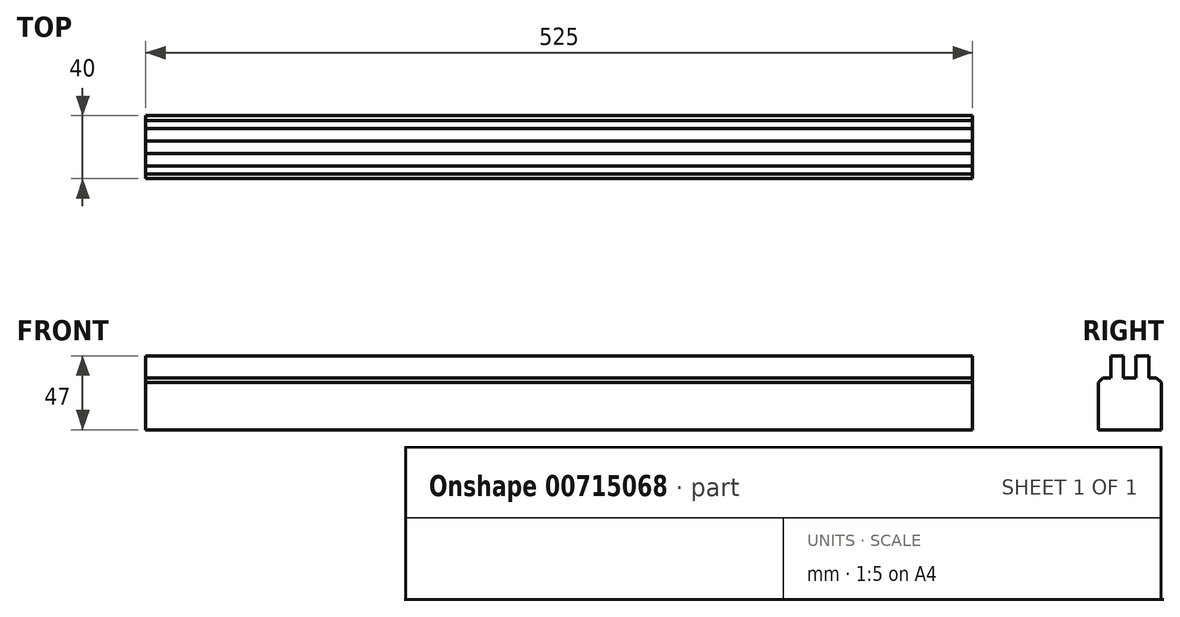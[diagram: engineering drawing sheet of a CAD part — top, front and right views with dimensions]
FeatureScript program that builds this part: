
annotation { "Feature Type Name" : "Feature", "Feature Type Description" : "" }
export const myFeature = defineFeature(function(context is Context, id is Id, definition is map)
    precondition{}
    {
        {
            var Q0;
            Q0=qCreatedBy(makeId("Right.planeOp"),FACE);
            var sketch = newSketch(context, id + "F0", { "sketchPlane" : qUnion([Q0])});
            skLineSegment(sketch, "E0", {"start": v(20, 63) * mm, "end": v(20, -63) * mm});
            skLineSegment(sketch, "E1", {"start": v(20, -63) * mm, "end": v(17, -66) * mm});
            skLineSegment(sketch, "E2", {"start": v(17, -66) * mm, "end": v(12, -66) * mm});
            skLineSegment(sketch, "E3", {"start": v(12, -52) * mm, "end": v(12, -66) * mm});
            skLineSegment(sketch, "E4", {"start": v(12, -52) * mm, "end": v(4, -52) * mm});
            skLineSegment(sketch, "E5", {"start": v(4, -66) * mm, "end": v(4, -52) * mm});
            skLineSegment(sketch, "E6", {"start": v(4, -66) * mm, "end": v(-4, -66) * mm});
            skLineSegment(sketch, "E7", {"start": v(-4, -52) * mm, "end": v(-4, -66) * mm});
            skLineSegment(sketch, "E8", {"start": v(-4, -52) * mm, "end": v(-12, -52) * mm});
            skLineSegment(sketch, "E9", {"start": v(-12, -66) * mm, "end": v(-12, -52) * mm});
            skLineSegment(sketch, "E10", {"start": v(-12, -66) * mm, "end": v(-17, -66) * mm});
            skLineSegment(sketch, "E11", {"start": v(-17, -66) * mm, "end": v(-20, -63) * mm});
            skLineSegment(sketch, "E12", {"start": v(-20, -63) * mm, "end": v(-20, 63) * mm});
            skLineSegment(sketch, "E13", {"start": v(-20, 63) * mm, "end": v(-17, 66) * mm});
            skLineSegment(sketch, "E14", {"start": v(-17, 66) * mm, "end": v(-12, 66) * mm});
            skLineSegment(sketch, "E15", {"start": v(-4, 66) * mm, "end": v(4, 66) * mm});
            skLineSegment(sketch, "E16", {"start": v(12, 66) * mm, "end": v(17, 66) * mm});
            skLineSegment(sketch, "E17", {"start": v(17, 66) * mm, "end": v(20, 63) * mm});
            skPoint(sketch, "E18.end.orphan", {"position": v(12, 57.8) * mm});
            skPoint(sketch, "E19.end.orphan", {"position": v(4, 66.3) * mm});
            skPoint(sketch, "E20.end.orphan", {"position": v(-4, 66.3) * mm});
            skLineSegment(sketch, "E21", {"start": v(-12, 66) * mm, "end": v(-12, 80) * mm});
            skLineSegment(sketch, "E22", {"start": v(-12, 80) * mm, "end": v(-4, 80) * mm});
            skLineSegment(sketch, "E23", {"start": v(-4, 80) * mm, "end": v(-4, 66) * mm});
            skLineSegment(sketch, "E24", {"start": v(4, 66) * mm, "end": v(4, 80) * mm});
            skLineSegment(sketch, "E25", {"start": v(4, 80) * mm, "end": v(12, 80) * mm});
            skLineSegment(sketch, "E26", {"start": v(12, 80) * mm, "end": v(12, 66) * mm});
            skLineSegment(sketch, "E27", {"start": v(20, -33) * mm, "end": v(-20, -33) * mm});
            skLineSegment(sketch, "E28", {"start": v(20, 33) * mm, "end": v(-20, 33) * mm});
            skPoint(sketch, "E29.end.orphan", {"position": v(-141.42, 0) * mm});
            skLineSegment(sketch, "E30", {"start": v(20, 0) * mm, "end": v(-20, 0) * mm});
            skLineSegment(sketch, "E31", {"start": v(20, 0) * mm, "end": v(-20, 0) * mm, "construction": true});
            skLineSegment(sketch, "E32", {"start": v(0, 33) * mm, "end": v(0, -33) * mm, "construction": true});
            skLineSegment(sketch, "E33", {"start": v(20, 14) * mm, "end": v(-20, 14) * mm});
            skSolve(sketch);
        }
        {
            var Q0;
            Q0=qCreatedBy(makeId("Front.planeOp"),FACE);
            var sketch = newSketch(context, id + "F1", { "sketchPlane" : qUnion([Q0])});
            skLineSegment(sketch, "E34", {"start": v(565, 0) * mm, "end": v(-565, 0) * mm, "construction": true});
            skPoint(sketch, "E35.right.start.orphan", {"position": v(-259.12, 108.1) * mm});
            skPoint(sketch, "E36.left.start.orphan", {"position": v(237.35, 108.1) * mm});
            skPoint(sketch, "E37.left.end.orphan", {"position": v(237.35, -84.05) * mm});
            skPoint(sketch, "E37.bottom.start.orphan", {"position": v(237.35, -117.05) * mm});
            skPoint(sketch, "E38.right.start.orphan", {"position": v(-259.12, -117.05) * mm});
            skPoint(sketch, "E38.top.end.orphan", {"position": v(-259.12, -84.05) * mm});
            skLineSegment(sketch, "E39.bottom", {"start": v(-605, 33) * mm, "end": v(-525, 33) * mm});
            skLineSegment(sketch, "E39.top", {"start": v(-605, 133) * mm, "end": v(-525, 133) * mm});
            skLineSegment(sketch, "E39.left", {"start": v(-605, 33) * mm, "end": v(-605, 133) * mm});
            skLineSegment(sketch, "E39.right", {"start": v(-525, 33) * mm, "end": v(-525, 133) * mm});
            skPoint(sketch, "E39.middle", {"position": v(-565, 83) * mm});
            skLineSegment(sketch, "E40.bottom", {"start": v(-605, -133) * mm, "end": v(-525, -133) * mm});
            skLineSegment(sketch, "E40.top", {"start": v(-605, -33) * mm, "end": v(-525, -33) * mm});
            skLineSegment(sketch, "E40.left", {"start": v(-605, -133) * mm, "end": v(-605, -33) * mm});
            skLineSegment(sketch, "E40.right", {"start": v(-525, -133) * mm, "end": v(-525, -33) * mm});
            skPoint(sketch, "E40.middle", {"position": v(-565, -83) * mm});
            skLineSegment(sketch, "E41.bottom", {"start": v(605, 33) * mm, "end": v(525, 33) * mm});
            skLineSegment(sketch, "E41.top", {"start": v(605, 133) * mm, "end": v(525, 133) * mm});
            skLineSegment(sketch, "E41.left", {"start": v(605, 33) * mm, "end": v(605, 133) * mm});
            skLineSegment(sketch, "E41.right", {"start": v(525, 33) * mm, "end": v(525, 133) * mm});
            skPoint(sketch, "E41.middle", {"position": v(565, 83) * mm});
            skLineSegment(sketch, "E42.bottom", {"start": v(605, -33) * mm, "end": v(525, -33) * mm});
            skLineSegment(sketch, "E42.top", {"start": v(605, -133) * mm, "end": v(525, -133) * mm});
            skLineSegment(sketch, "E42.left", {"start": v(605, -33) * mm, "end": v(605, -133) * mm});
            skLineSegment(sketch, "E42.right", {"start": v(525, -33) * mm, "end": v(525, -133) * mm});
            skPoint(sketch, "E42.middle", {"position": v(565, -83) * mm});
            skSolve(sketch);
        }
        {
            var Q0;
            {var subQ0=sQuery(id+"F0.wireOp",EDGE,"E28");Q0=makeQuery(id+"F0.imprint","IMPRINT",FACE,{"disambiguationData":[TD([[makeQuery(id+"F0.imprint","IMPRINT",EDGE,{"derivedFrom":subQ0}),1.0]])]});}
            var Q1;
            {var subQ3=sQuery(id+"F0.wireOp",EDGE,"E13");Q1=makeQuery(id+"F0.imprint","IMPRINT",FACE,{"disambiguationData":[TD([[makeQuery(id+"F0.imprint","IMPRINT",EDGE,{"derivedFrom":subQ3}),-1.0]])]});}
            extrude(context, id + "F2", {"entities" : qUnion([Q0, Q1]), "oppositeDirection" : true, "depth" : 565 * mm, "offsetDistance" : 25 * mm});
        }
        {
            var Q0;
            Q0=makeQuery(id+"F1.imprint","IMPRINT",FACE,{"disambiguationData":[TD([[makeQuery(id+"F1.imprint","IMPRINT",EDGE,{"derivedFrom":sQuery(id+"F1.wireOp",EDGE,"E39.bottom")}),1.0]])]});
            extrude(context, id + "F3", {"entities" : qUnion([Q0]), "operationType" : NewBodyOperationType.REMOVE, "endBound" : BoundingType.SYMMETRIC, "oppositeDirection" : true, "depth" : 50 * mm, "offsetDistance" : 25 * mm});
        }
        {
            var Q0;
            Q0=makeQuery(id+"F2.opExtrude","SWEPT_FACE",FACE,{"disambiguationData":[OSD([sQuery(id+"F0.wireOp",EDGE,"E12")])]});
            var sketch = newSketch(context, id + "F4", { "sketchPlane" : qUnion([Q0])});
            skLineSegment(sketch, "E43.bottom", {"start": v(-565, 33) * mm, "end": v(0, 33) * mm});
            skLineSegment(sketch, "E43.top", {"start": v(-565, 14) * mm, "end": v(0, 14) * mm});
            skLineSegment(sketch, "E43.left", {"start": v(-565, 33) * mm, "end": v(-565, 14) * mm});
            skLineSegment(sketch, "E43.right", {"start": v(0, 33) * mm, "end": v(0, 14) * mm});
            skSolve(sketch);
        }
        {
            var Q0;
            Q0=makeQuery(id+"F4.imprint","IMPRINT",FACE,{"disambiguationData":[TD([[makeQuery(id+"F4.imprint","IMPRINT",EDGE,{"derivedFrom":sQuery(id+"F4.wireOp",EDGE,"E43.top")}),1.0]])]});
            extrude(context, id + "F5", {"entities" : qUnion([Q0]), "operationType" : NewBodyOperationType.REMOVE, "endBound" : BoundingType.UP_TO_NEXT, "oppositeDirection" : true, "depth" : 25 * mm, "offsetDistance" : 25 * mm});
        }
    });
